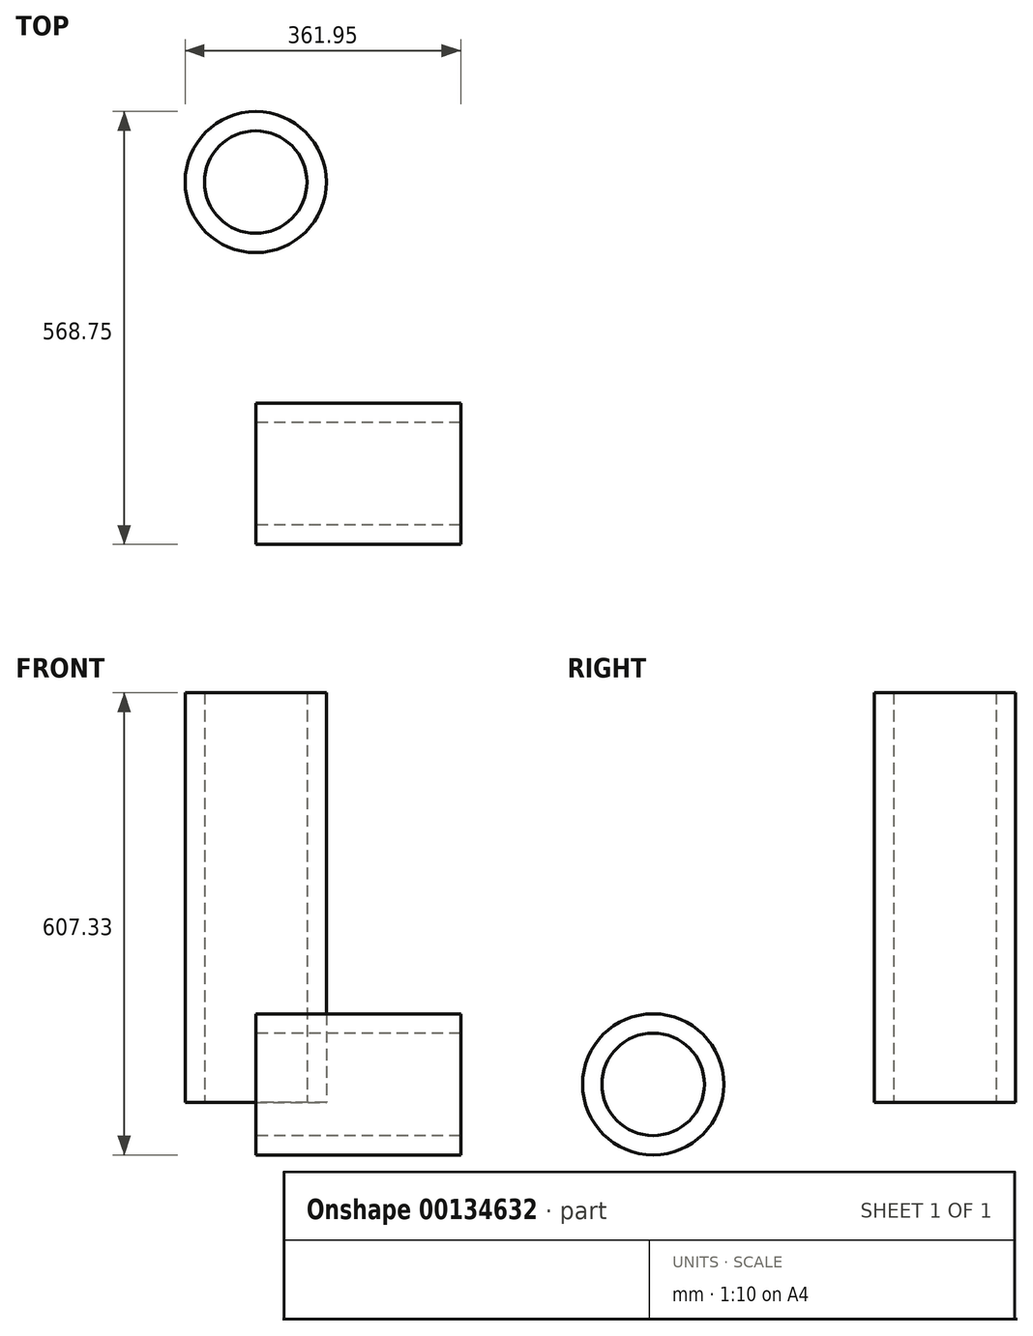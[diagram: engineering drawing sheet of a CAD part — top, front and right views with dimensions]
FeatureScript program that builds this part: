
annotation { "Feature Type Name" : "Feature", "Feature Type Description" : "" }
export const myFeature = defineFeature(function(context is Context, id is Id, definition is map)
    precondition{}
    {
        {
            var Q0;
            Q0=qCreatedBy(makeId("Top.planeOp"),FACE);
            var sketch = newSketch(context, id + "F0", { "sketchPlane" : qUnion([Q0])});
            skCircle(sketch, "E0", {"center": v(0, 0) * mm, "radius": 92.7 * mm});
            skSolve(sketch);
        }
        {
            var Q0;
            Q0=makeQuery(id+"F0.imprint","IMPRINT",FACE,{"disambiguationData":[TD([[makeQuery(id+"F0.imprint","IMPRINT",EDGE,{"derivedFrom":sQuery(id+"F0.wireOp",EDGE,"E0")}),1.0]])]});
            var Q1;
            Q1=sQuery(id+"F0.wireOp",EDGE,"E0");
            extrude(context, id + "F1", {"entities" : qUnion([Q0]), "surfaceEntities" : qUnion([Q1]), "depth" : 538.48 * mm});
        }
        {
            var Q0;
            Q0=qCreatedBy(makeId("Right.planeOp"),FACE);
            var sketch = newSketch(context, id + "F2", { "sketchPlane" : qUnion([Q0])});
            skCircle(sketch, "E1", {"center": v(-383.33, 23.86) * mm, "radius": 92.7 * mm});
            skSolve(sketch);
        }
        {
            var Q0;
            Q0=makeQuery(id+"F2.imprint","IMPRINT",FACE,{"disambiguationData":[TD([[makeQuery(id+"F2.imprint","IMPRINT",EDGE,{"derivedFrom":sQuery(id+"F2.wireOp",EDGE,"E1")}),1.0]])]});
            var Q1;
            Q1=sQuery(id+"F2.wireOp",EDGE,"E1");
            extrude(context, id + "F3", {"entities" : qUnion([Q0]), "surfaceEntities" : qUnion([Q1]), "depth" : 269.24 * mm});
        }
        {
            var Q0;
            Q0=makeQuery(id+"F1.opExtrude","CAP_FACE",FACE,{"disambiguationData":[OSD([sQuery(id+"F0.wireOp",EDGE,"E0")])],"isStart":false});
            var Q1;
            Q1=makeQuery(id+"F1.opExtrude","CAP_FACE",FACE,{"disambiguationData":[OSD([sQuery(id+"F0.wireOp",EDGE,"E0")])],"isStart":true});
            var Q2;
            Q2=makeQuery(id+"F3.opExtrude","CAP_FACE",FACE,{"disambiguationData":[OSD([sQuery(id+"F2.wireOp",EDGE,"E1")])],"isStart":false});
            var Q3;
            Q3=makeQuery(id+"F3.opExtrude","CAP_FACE",FACE,{"disambiguationData":[OSD([sQuery(id+"F2.wireOp",EDGE,"E1")])],"isStart":true});
            shell(context, id + "F4", {"entities" : qUnion([Q0, Q1, Q2, Q3]), "thickness" : 25.4 * mm});
        }
    });
